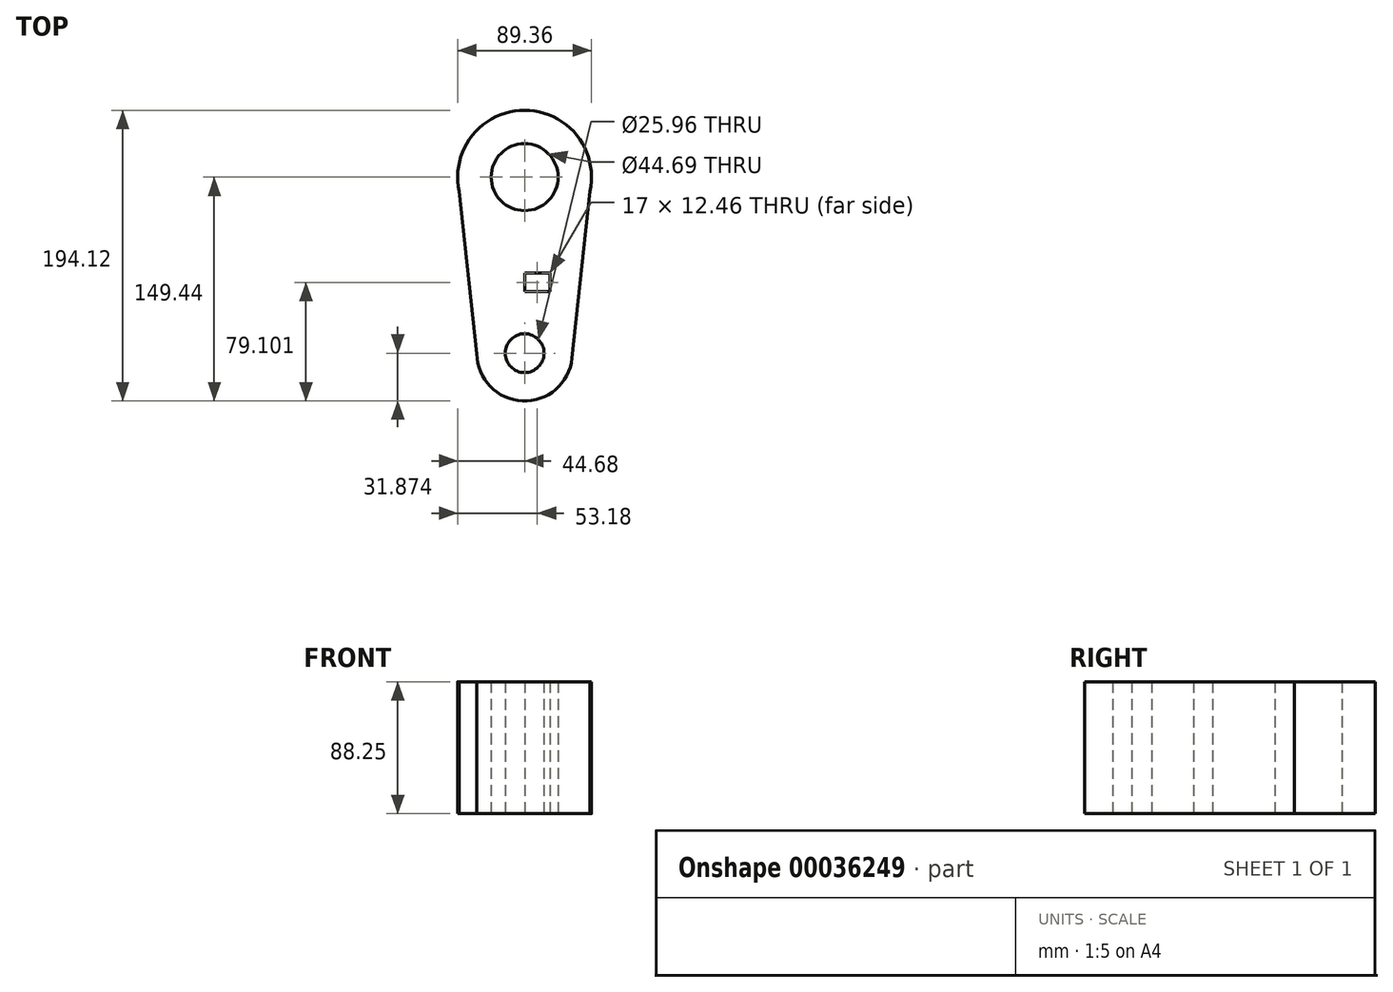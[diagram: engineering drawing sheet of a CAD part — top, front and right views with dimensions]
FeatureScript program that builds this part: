
annotation { "Feature Type Name" : "Feature", "Feature Type Description" : "" }
export const myFeature = defineFeature(function(context is Context, id is Id, definition is map)
    precondition{}
    {
        {
            var Q0;
            Q0=qCreatedBy(makeId("Top.planeOp"),FACE);
            cPlane(context, id + "F0", {"entities" : qUnion([Q0]), "cplaneType" : CPlaneType.OFFSET, "offset" : 152.4 * mm, "width" : 152.4 * mm, "height" : 152.4 * mm});
        }
        {
            var Q0;
            Q0=qCreatedBy(id+"F0.planeOp",FACE);
            var sketch = newSketch(context, id + "F1", { "sketchPlane" : qUnion([Q0])});
            skCircle(sketch, "E0", {"center": v(0, 0) * mm, "radius": 44.68 * mm});
            skCircle(sketch, "E1", {"center": v(0, -117.57) * mm, "radius": 31.88 * mm});
            skLineSegment(sketch, "E2", {"start": v(-44.68, 0) * mm, "end": v(-31.23, -123.98) * mm});
            skLineSegment(sketch, "E3", {"start": v(44.68, 0) * mm, "end": v(31.37, -123.98) * mm});
            skCircle(sketch, "E4", {"center": v(0, 0) * mm, "radius": 22.34 * mm});
            skCircle(sketch, "E5", {"center": v(0, -117.57) * mm, "radius": 12.98 * mm});
            skLineSegment(sketch, "E6.bottom", {"start": v(0, -64.1) * mm, "end": v(17, -64.1) * mm});
            skLineSegment(sketch, "E6.top", {"start": v(0, -76.57) * mm, "end": v(17, -76.57) * mm});
            skLineSegment(sketch, "E6.left", {"start": v(0, -64.1) * mm, "end": v(0, -76.57) * mm});
            skLineSegment(sketch, "E6.right", {"start": v(17, -64.1) * mm, "end": v(17, -76.57) * mm});
            skSolve(sketch);
        }
        {
            var Q0;
            Q0 = qSketchRegion(id + "F1", true);
            extrude(context, id + "F2", {"entities" : qUnion([Q0]), "depth" : 88.25 * mm});
        }
    });
